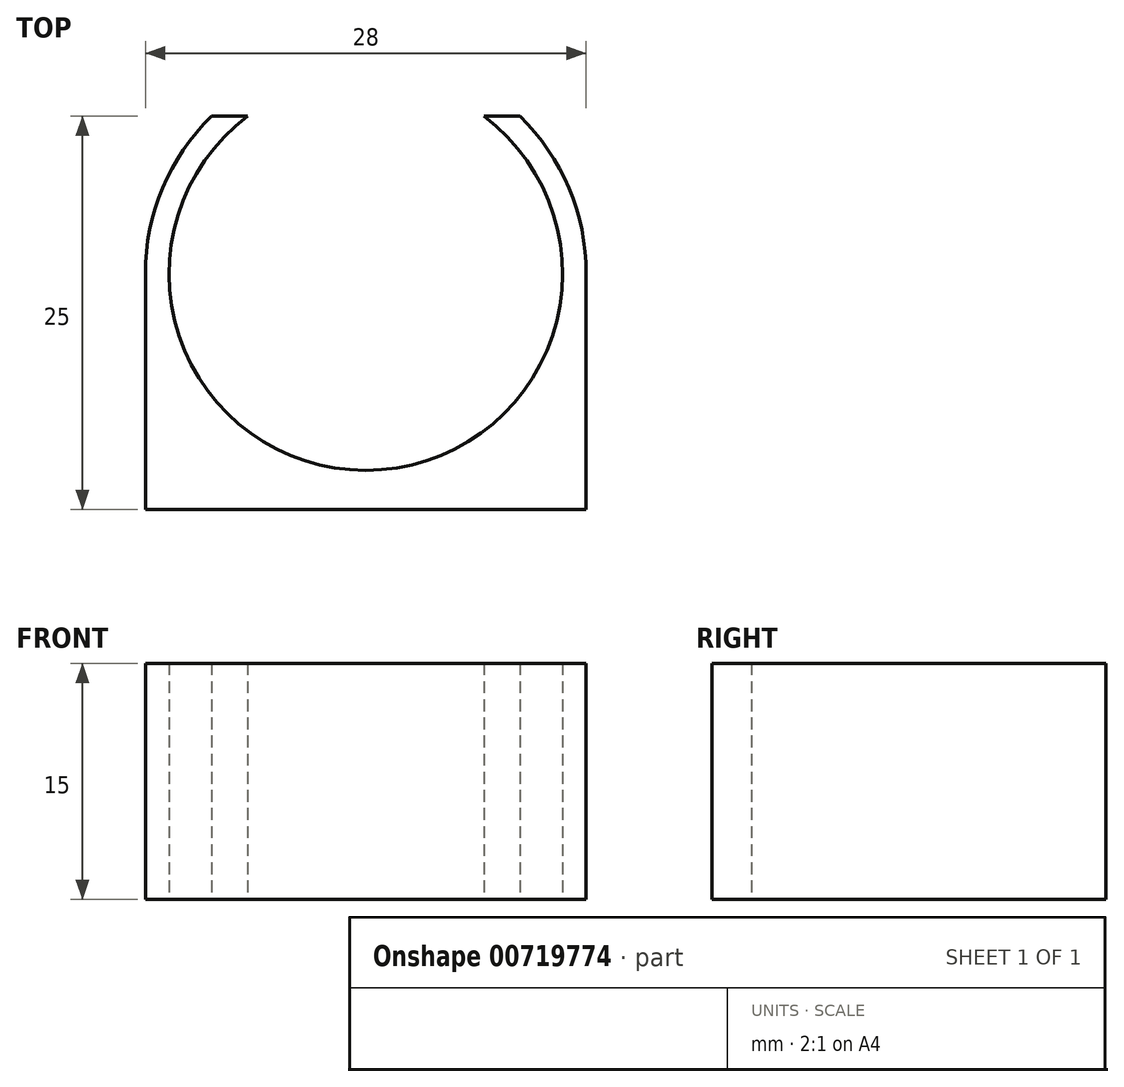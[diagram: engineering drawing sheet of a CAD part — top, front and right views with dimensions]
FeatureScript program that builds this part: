
annotation { "Feature Type Name" : "Feature", "Feature Type Description" : "" }
export const myFeature = defineFeature(function(context is Context, id is Id, definition is map)
    precondition{}
    {
        {
            var Q0;
            Q0=qCreatedBy(makeId("Top.planeOp"),FACE);
            var sketch = newSketch(context, id + "F0", { "sketchPlane" : qUnion([Q0])});
            skArc(sketch, "E0", {"start": v(6.5, 25) * mm, "mid": v(14, 2.5) * mm, "end": v(21.5, 25) * mm});
            skArc(sketch, "E1", {"start": v(4.2, 25) * mm, "mid": v(1.1, 20.42) * mm, "end": v(0, 15) * mm});
            skLineSegment(sketch, "E2", {"start": v(0, 15) * mm, "end": v(0, 0) * mm});
            skLineSegment(sketch, "E3", {"start": v(4.2, 25) * mm, "end": v(23.8, 25) * mm});
            skLineSegment(sketch, "E4", {"start": v(28, 15) * mm, "end": v(28, 0) * mm});
            skLineSegment(sketch, "E5", {"start": v(28, 0) * mm, "end": v(0, 0) * mm});
            skArc(sketch, "E6.trimOffspring", {"start": v(28, 15) * mm, "mid": v(26.9, 20.42) * mm, "end": v(23.8, 25) * mm});
            skSolve(sketch);
        }
        {
            var Q0;
            {var subQ1=sQuery(id+"F0.wireOp",EDGE,"E0");Q0=makeQuery(id+"F0.imprint","IMPRINT",FACE,{"disambiguationData":[TD([[makeQuery(id+"F0.imprint","IMPRINT",EDGE,{"derivedFrom":subQ1}),-1.0]])]});}
            extrude(context, id + "F1", {"entities" : qUnion([Q0]), "depth" : 15 * mm, "offsetDistance" : 25 * mm});
        }
    });
